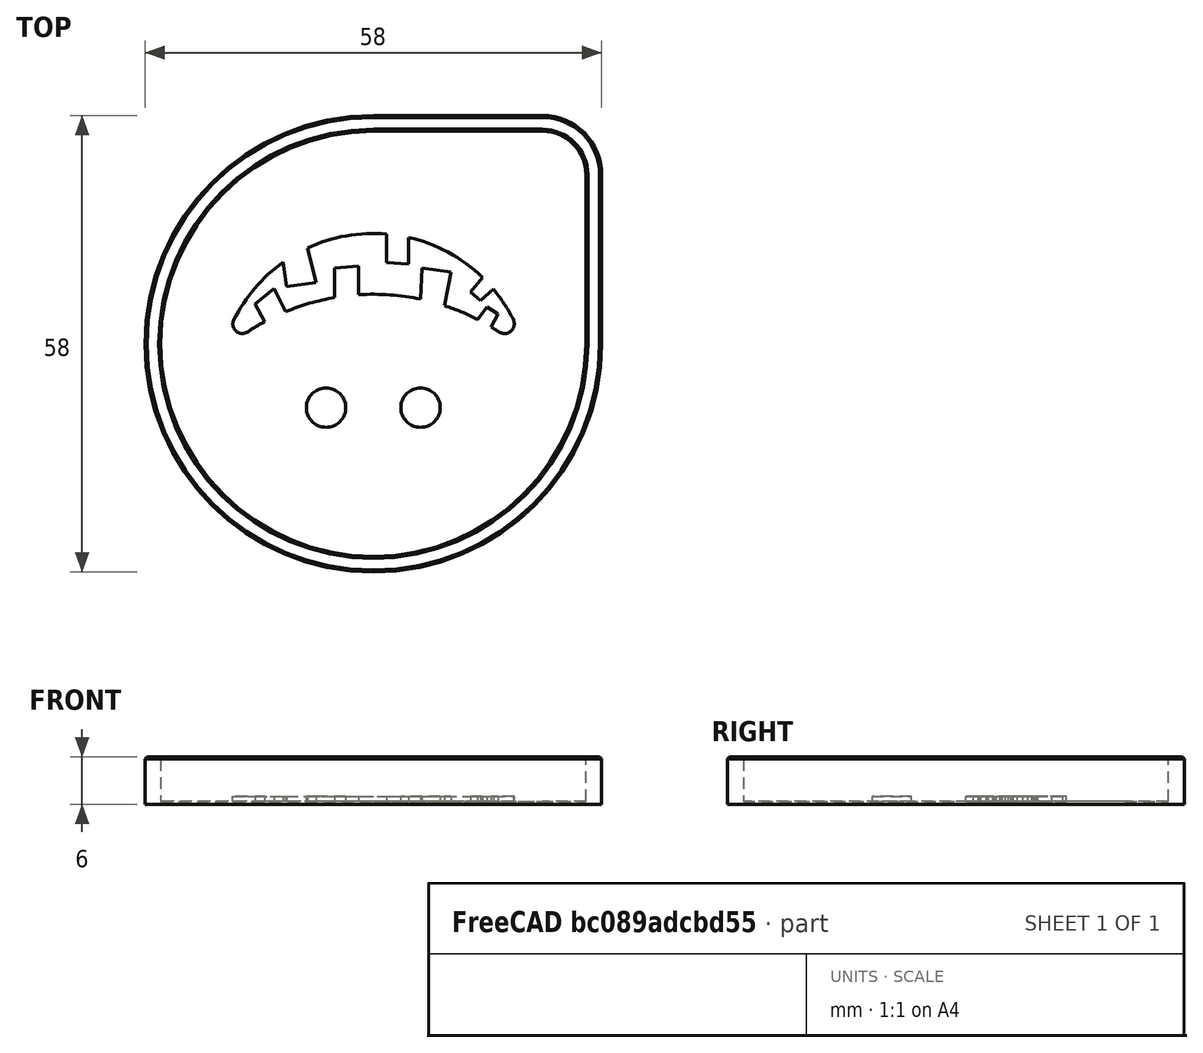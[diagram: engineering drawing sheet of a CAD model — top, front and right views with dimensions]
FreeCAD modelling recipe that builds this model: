
FCSTD DOCUMENT  (FreeCAD 0.19R22262 (Git))
Label: abdeckung_nachtlicht
License: All rights reserved
LicenseURL: http://en.wikipedia.org/wiki/All_rights_reserved
objects: Sketcher::SketchObject×3, PartDesign::Pad×2, PartDesign::Chamfer×2, Image::ImagePlane×1, PartDesign::AdditivePipe×1, PartDesign::Body×1, Mesh::Feature×1
note: 14 computed .brp shape members not serialized (recipe doc carries the construction recipe); baked Part::Feature solids carry a one-line shape summary decoded from their .brp

FEATURE [Sketcher::SketchObject] Sketch
  MapMode = 5
  Support = -> [XY_Plane]
  sketch-geometry (4):
    g0: LineSegment StartX=27 StartY=21.5 StartZ=0 EndX=27 EndY=-3.6e-15 EndZ=0
    g1: ArcOfCircle CenterX=0 CenterY=0 CenterZ=0 NormalX=0 NormalY=0 NormalZ=1 AngleXU=0 Radius=27 StartAngle=1.5708 EndAngle=6.28319
    g2: LineSegment StartX=1.5964e-12 StartY=27 StartZ=0 EndX=21.5 EndY=27 EndZ=0
    g3: ArcOfCircle CenterX=21.5 CenterY=21.5 CenterZ=0 NormalX=0 NormalY=0 NormalZ=1 AngleXU=0 Radius=5.5 StartAngle=0 EndAngle=1.5708
  constraints (9):
    c: Vertical(g0)
    c: Tangent(g2,g3) = 1.5708
    c: Horizontal(g2)
    c: Tangent(g0,g3) = 1.5708
    c: Radius(g3) = 5.5
    c: DistanceX(g0) = 27
    c: Tangent(g0,g1) = 1.5708
    c: Tangent(g1,g2) = 1.5708
    c: Coincident(g1,g-1)
FEATURE [Image::ImagePlane] ImagePlane
  XSize = 60
  YSize = 61
FEATURE [PartDesign::Pad] Pad
  Length = 0.4
  Length2 = 100
  Profile = -> Sketch
  Refine = true
  Type = 0
FEATURE [Sketcher::SketchObject] Sketch001
  ExternalGeometry = -> [Pad]
  MapMode = 5
  Placement = pos=(0,0,0) rot=(0.57735,0.57735,0.57735;2.0944rad)
  Support = -> [YZ_Plane]
  sketch-geometry (4):
    g0: LineSegment StartX=27 StartY=6 StartZ=0 EndX=29 EndY=6 EndZ=0
    g1: LineSegment StartX=29 StartY=6 StartZ=0 EndX=29 EndY=0 EndZ=0
    g2: LineSegment StartX=29 StartY=0 StartZ=0 EndX=27 EndY=0 EndZ=0
    g3: LineSegment StartX=27 StartY=0 StartZ=0 EndX=27 EndY=6 EndZ=0
  constraints (12):
    c: Coincident(g0,g1)
    c: Coincident(g1,g2)
    c: Coincident(g2,g3)
    c: Coincident(g3,g0)
    c: Horizontal(g0)
    c: Horizontal(g2)
    c: Vertical(g1)
    c: Vertical(g3)
    c: Vertical(g2,g-3)
    c: DistanceX(g0,g0) = 2
    c: DistanceY(g1,g1) = 6
    c: Horizontal(g1,g-1)
FEATURE [PartDesign::AdditivePipe] AdditivePipe
  AuxilleryCurvelinear = true
  AuxillerySpineTangent = false
  BaseFeature = -> Pad
  Binormal = (0,0,0)
  Mode = 0
  Profile = -> Sketch001
  Refine = true
  Spine = -> Pad [Edge10,Edge12,Edge4,Edge7]
  SpineTangent = false
  Transformation = 0
  Transition = 0
FEATURE [PartDesign::Chamfer] Chamfer
  Angle = 45
  Base = -> AdditivePipe [Edge13,Edge14,Edge15,Edge16]
  BaseFeature = -> AdditivePipe
  ChamferType = 0
  FlipDirection = false
  Refine = true
  Size = 0.25
  Size2 = 1
  SupportTransform = false
FEATURE [PartDesign::Chamfer] Chamfer001
  Angle = 45
  Base = -> Chamfer [Edge7,Edge8,Edge6,Edge5]
  BaseFeature = -> Chamfer
  ChamferType = 0
  FlipDirection = false
  Refine = true
  Size = 0.25
  Size2 = 1
  SupportTransform = false
FEATURE [Sketcher::SketchObject] Sketch002
  AttachmentOffset = pos=(0,0,-1) rot=(0,0,1;0rad)
  MapMode = 5
  Placement = pos=(0,0,1) rot=(1,0,0;3.14159rad)
  Support = -> [Chamfer001]
  sketch-geometry (34):
    g0: Circle CenterX=-6 CenterY=8.10803 CenterZ=0 NormalX=0 NormalY=0 NormalZ=1 AngleXU=0 Radius=2.5
    g1: Circle CenterX=6 CenterY=8.10803 CenterZ=0 NormalX=0 NormalY=0 NormalZ=1 AngleXU=0 Radius=2.5
    g2: ArcOfCircle CenterX=0 CenterY=22.8202 CenterZ=0 NormalX=0 NormalY=0 NormalZ=1 AngleXU=0 Radius=29.1153 StartAngle=4.13069 EndAngle=4.21805
    g3: ArcOfCircle CenterX=0.0483038 CenterY=5.82017 CenterZ=0 NormalX=0 NormalY=0 NormalZ=1 AngleXU=0 Radius=19.8511 StartAngle=3.60392 EndAngle=4.09518
    g4: ArcOfCircle CenterX=16.6783 CenterY=-2.54033 CenterZ=0 NormalX=0 NormalY=0 NormalZ=1 AngleXU=0 Radius=1.2379 StartAngle=5.83016 EndAngle=8.43651
    g5: ArcOfCircle CenterX=-16.6521 CenterY=-2.50238 CenterZ=0 NormalX=0 NormalY=0 NormalZ=1 AngleXU=0 Radius=1.19181 StartAngle=0.989098 EndAngle=3.60392
    g6: LineSegment StartX=-4.91211 StartY=-5.87782 StartZ=0 EndX=-4.91211 EndY=-9.63265 EndZ=0
    g7: LineSegment StartX=-4.91211 StartY=-9.63265 StartZ=0 EndX=-1.84738 EndY=-9.8601 EndZ=0
    g8: LineSegment StartX=-1.84738 StartY=-9.8601 StartZ=0 EndX=-1.84738 EndY=-6.23651 EndZ=0
    g9: LineSegment StartX=1.70779 StartY=-13.9614 StartZ=0 EndX=1.70779 EndY=-10.3463 EndZ=0
    g10: LineSegment StartX=1.70779 StartY=-10.3463 StartZ=0 EndX=4.4723 EndY=-10.1208 EndZ=0
    g11: LineSegment StartX=4.4723 StartY=-10.1208 StartZ=0 EndX=4.4723 EndY=-13.5317 EndZ=0
    g12: ArcOfCircle CenterX=0.0483038 CenterY=5.82017 CenterZ=0 NormalX=0 NormalY=0 NormalZ=1 AngleXU=0 Radius=19.8511 StartAngle=4.93714 EndAngle=5.48147
    g13: ArcOfCircle CenterX=0 CenterY=22.8202 CenterZ=0 NormalX=0 NormalY=0 NormalZ=1 AngleXU=0 Radius=29.1153 StartAngle=4.6489 EndAngle=4.92094
    g14: LineSegment StartX=-11.4407 StartY=-10.3683 StartZ=0 EndX=-11.0385 EndY=-7.26647 EndZ=0
    g15: LineSegment StartX=-11.0385 StartY=-7.26647 StartZ=0 EndX=-7.25417 EndY=-7.77105 EndZ=0
    g16: LineSegment StartX=-7.25417 StartY=-7.77105 StartZ=0 EndX=-8.35016 EndY=-12.1668 EndZ=0
    g17: ArcOfCircle CenterX=0.0483038 CenterY=5.82017 CenterZ=0 NormalX=0 NormalY=0 NormalZ=1 AngleXU=0 Radius=19.8511 StartAngle=4.27555 EndAngle=4.79608
    g18: LineSegment StartX=6.02803 StartY=-5.66432 StartZ=0 EndX=6.20139 EndY=-9.62119 EndZ=0
    g19: LineSegment StartX=6.20139 StartY=-9.62119 StartZ=0 EndX=9.90165 EndY=-9.1166 EndZ=0
    g20: LineSegment StartX=9.90165 StartY=-9.1166 StartZ=0 EndX=9.06161 EndY=-4.84914 EndZ=0
    g21: ArcOfCircle CenterX=0 CenterY=22.8202 CenterZ=0 NormalX=0 NormalY=0 NormalZ=1 AngleXU=0 Radius=29.1153 StartAngle=5.02888 EndAngle=5.18462
    g22: LineSegment StartX=-13.8137 StartY=-2.80958 StartZ=0 EndX=-14.9911 EndY=-5.07994 EndZ=0
    g23: LineSegment StartX=-14.9911 StartY=-5.07994 StartZ=0 EndX=-12.6364 EndY=-7.01417 EndZ=0
    g24: LineSegment StartX=-12.6364 StartY=-7.01417 StartZ=0 EndX=-11.1405 EndY=-4.0795 EndZ=0
    g25: LineSegment StartX=13.8542 StartY=-8.44383 StartZ=0 EndX=12.3405 EndY=-6.59369 EndZ=0
    g26: LineSegment StartX=12.3405 StartY=-6.59369 StartZ=0 EndX=13.5984 EndY=-5.51558 EndZ=0
    g27: LineSegment StartX=13.5984 StartY=-5.51558 StartZ=0 EndX=15.2542 EndY=-6.94089 EndZ=0
    g28: ArcOfCircle CenterX=0 CenterY=22.8202 CenterZ=0 NormalX=0 NormalY=0 NormalZ=1 AngleXU=0 Radius=29.1153 StartAngle=4.31974 EndAngle=4.54287
    g29: ArcOfCircle CenterX=0.0483038 CenterY=5.82017 CenterZ=0 NormalX=0 NormalY=0 NormalZ=1 AngleXU=0 Radius=19.8511 StartAngle=5.58499 EndAngle=5.81815
    g30: LineSegment StartX=13.2438 StartY=-3.10867 StartZ=0 EndX=14.4502 EndY=-4.67108 EndZ=0
    g31: LineSegment StartX=14.4502 StartY=-4.67108 StartZ=0 EndX=15.8729 EndY=-3.8061 EndZ=0
    g32: LineSegment StartX=15.8729 StartY=-3.8061 StartZ=0 EndX=14.9852 EndY=-2.14277 EndZ=0
    g33: ArcOfCircle CenterX=0 CenterY=22.8202 CenterZ=0 NormalX=0 NormalY=0 NormalZ=1 AngleXU=0 Radius=29.1153 StartAngle=5.25303 EndAngle=5.29409
  constraints (57):
    c: Symmetric(g0,g1,g-2)
    c: Equal(g0,g1)
    c: Radius(g0) = 2.5
    c: PointOnObject(g2,g-2)
    c: Horizontal(g33,g2)
    c: DistanceX(g0,g-1) = 6
    c: DistanceY(g3,g2) = 17
    c: Coincident(g33,g4) = 1.5708
    c: Coincident(g29,g4) = -1.5708
    c: Tangent(g3,g5) = -1.5708
    c: Tangent(g2,g5) = 1.5708
    c: Vertical(g6)
    c: Coincident(g6,g7)
    c: Coincident(g7,g8)
    c: Vertical(g8)
    c: Coincident(g9,g10)
    c: Coincident(g10,g11)
    c: Vertical(g11)
    c: Vertical(g9)
    c: Equal(g3,g12)
    c: Coincident(g17,g9)
    c: Coincident(g12,g11)
    c: Coincident(g3,g12)
    c: Equal(g2,g13)
    c: Coincident(g28,g6)
    c: Coincident(g13,g8)
    c: Coincident(g2,g13)
    c: Coincident(g14,g15)
    c: Coincident(g15,g16)
    c: Equal(g3,g17)
    c: Coincident(g3,g14)
    c: Coincident(g17,g16)
    c: Coincident(g3,g17)
    c: Coincident(g18,g19)
    c: Coincident(g19,g20)
    c: Equal(g13,g21)
    c: Coincident(g13,g18)
    c: Coincident(g21,g20)
    c: Coincident(g13,g21)
    c: Coincident(g22,g23)
    c: Coincident(g23,g24)
    c: Coincident(g25,g26)
    c: Coincident(g26,g27)
    c: Equal(g2,g28)
    c: Coincident(g2,g22)
    c: Coincident(g28,g24)
    c: Coincident(g2,g28)
    c: Equal(g12,g29)
    c: Coincident(g12,g25)
    c: Coincident(g29,g27)
    c: Coincident(g12,g29)
    c: Coincident(g30,g31)
    c: Coincident(g31,g32)
    c: Equal(g21,g33)
    c: Coincident(g21,g30)
    c: Coincident(g33,g32)
    c: Coincident(g21,g33)
FEATURE [PartDesign::Pad] Pad001
  BaseFeature = -> Chamfer001
  Length = 1
  Length2 = 100
  Profile = -> Sketch002
  Refine = true
  Type = 2
FEATURE [PartDesign::Body] Body
  Group = -> [Sketch,Pad,Sketch001,AdditivePipe,Chamfer,Chamfer001,Sketch002,Pad001]
  Origin = -> Origin
  Tip = -> Pad001
FEATURE [Mesh::Feature] Mesh  label="Pad001 (Meshed)"
